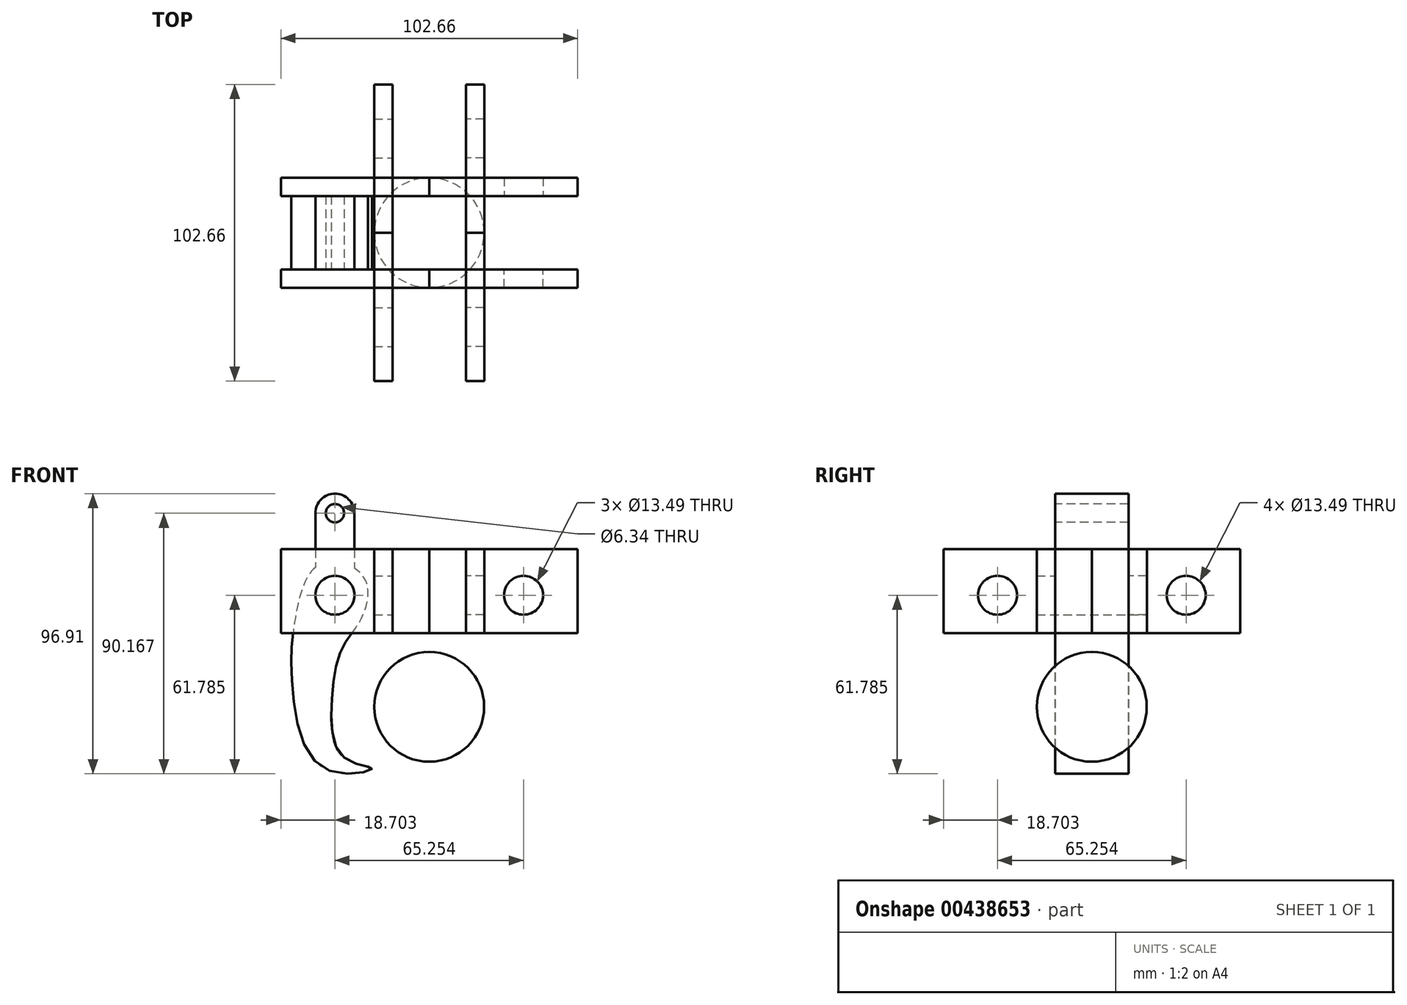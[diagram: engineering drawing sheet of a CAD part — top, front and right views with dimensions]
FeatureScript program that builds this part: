
annotation { "Feature Type Name" : "Feature", "Feature Type Description" : "" }
export const myFeature = defineFeature(function(context is Context, id is Id, definition is map)
    precondition{}
    {
        {
            var Q0;
            Q0=qCreatedBy(makeId("Front.planeOp"),FACE);
            var sketch = newSketch(context, id + "F0", { "sketchPlane" : qUnion([Q0])});
            skCircle(sketch, "E0", {"center": v(0, 0) * mm, "radius": 19 * mm});
            skFitSpline(sketch, "E1", {"points": [v(-14.63, -20) * mm, v(-23.81, -17.55) * mm, v(-30.46, 0) * mm, v(-28.59, 20.45) * mm, v(-23.1, 30.72) * mm, v(-23.1, 45.51) * mm, v(-38.56, 48.92) * mm, v(-45.55, 30.12) * mm, v(-45.15, 10.11) * mm, v(-30.93, -21.5) * mm, v(-14.63, -20) * mm]});
            skCircle(sketch, "E2", {"center": v(-32.63, 38.62) * mm, "radius": 6.75 * mm});
            skSolve(sketch);
        }
        {
            var Q0;
            Q0=makeQuery(id+"F0.imprint","IMPRINT",FACE,{"disambiguationData":[TD([[makeQuery(id+"F0.imprint","IMPRINT",EDGE,{"derivedFrom":sQuery(id+"F0.wireOp",EDGE,"E1")}),1.0]])]});
            extrude(context, id + "F1", {"entities" : qUnion([Q0]), "depth" : 12.7 * mm});
        }
        {
            var Q0;
            Q0=makeQuery(id+"F1.opExtrude","CAP_FACE",FACE,{"disambiguationData":[OSD([sQuery(id+"F0.wireOp",EDGE,"E1"),sQuery(id+"F0.wireOp",EDGE,"E2")])],"isStart":false});
            var sketch = newSketch(context, id + "F2", { "sketchPlane" : qUnion([Q0])});
            skLineSegment(sketch, "E3.bottom", {"start": v(0, 54.58) * mm, "end": v(-51.33, 54.58) * mm});
            skLineSegment(sketch, "E3.top", {"start": v(0, 25.55) * mm, "end": v(-51.33, 25.55) * mm});
            skLineSegment(sketch, "E3.left", {"start": v(0, 54.58) * mm, "end": v(0, 25.55) * mm});
            skLineSegment(sketch, "E3.right", {"start": v(-51.33, 54.58) * mm, "end": v(-51.33, 25.55) * mm});
            skSolve(sketch);
        }
        {
            var Q0;
            Q0=makeQuery(id+"F2.imprint","IMPRINT",FACE,{"disambiguationData":[TD([[makeQuery(id+"F2.imprint","IMPRINT",EDGE,{"derivedFrom":sQuery(id+"F2.wireOp",EDGE,"E3.bottom")}),1.0]])]});
            var Q1;
            Q1=makeQuery(id+"F2.imprint","IMPRINT",FACE,{"disambiguationData":[TD([[makeQuery(id+"F2.imprint","IMPRINT",EDGE,{"derivedFrom":makeQuery(id+"F1.opExtrude","CAP_EDGE",EDGE,{"disambiguationData":[OSD([sQuery(id+"F0.wireOp",EDGE,"E2")])],"isStart":false})}),-1.0]])]});
            extrude(context, id + "F3", {"entities" : qUnion([Q0, Q1]), "depth" : 6.35 * mm});
        }
        {
            var Q0;
            Q0=makeQuery(id+"F1.opExtrude","SWEPT_BODY",BODY,{"disambiguationData":[OSD([sQuery(id+"F0.wireOp",EDGE,"E1"),sQuery(id+"F0.wireOp",EDGE,"E2")])]});
            var Q1;
            Q1=makeQuery(id+"F3.opExtrude","SWEPT_BODY",BODY,{"disambiguationData":[OSD([sQuery(id+"F0.wireOp",EDGE,"E2"),sQuery(id+"F2.wireOp",EDGE,"E3.bottom"),sQuery(id+"F2.wireOp",EDGE,"E3.top"),sQuery(id+"F2.wireOp",EDGE,"E3.left"),sQuery(id+"F2.wireOp",EDGE,"E3.right")])]});
            var Q2;
            Q2=qCreatedBy(makeId("Front.planeOp"),FACE);
            mirror(context, id + "F4", {"entities" : qUnion([Q0, Q1]), "mirrorPlane" : qUnion([Q2])});
        }
        {
            var Q0;
            Q0=makeQuery(id+"F3.opExtrude","SWEPT_BODY",BODY,{"disambiguationData":[OSD([sQuery(id+"F0.wireOp",EDGE,"E2"),sQuery(id+"F2.wireOp",EDGE,"E3.bottom"),sQuery(id+"F2.wireOp",EDGE,"E3.top"),sQuery(id+"F2.wireOp",EDGE,"E3.left"),sQuery(id+"F2.wireOp",EDGE,"E3.right")])]});
            var Q1;
            Q1=makeQuery(id+"F4.opPattern","COPY",BODY,{"derivedFrom":makeQuery(id+"F3.opExtrude","SWEPT_BODY",BODY,{"disambiguationData":[OSD([sQuery(id+"F0.wireOp",EDGE,"E2"),sQuery(id+"F2.wireOp",EDGE,"E3.bottom"),sQuery(id+"F2.wireOp",EDGE,"E3.top"),sQuery(id+"F2.wireOp",EDGE,"E3.left"),sQuery(id+"F2.wireOp",EDGE,"E3.right")])]}),"instanceName":"1"});
            var Q2;
            Q2=qCreatedBy(makeId("Right.planeOp"),FACE);
            mirror(context, id + "F5", {"entities" : qUnion([Q0, Q1]), "mirrorPlane" : qUnion([Q2])});
        }
        {
            var Q0;
            Q0=qCreatedBy(makeId("Front.planeOp"),FACE);
            var sketch = newSketch(context, id + "F6", { "sketchPlane" : qUnion([Q0])});
            skLineSegment(sketch, "E4", {"start": v(0, 0) * mm, "end": v(0, 97.35) * mm, "construction": true});
            skSolve(sketch);
        }
        {
            var Q0;
            Q0=makeQuery(id+"F3.opExtrude","SWEPT_BODY",BODY,{"disambiguationData":[OSD([sQuery(id+"F0.wireOp",EDGE,"E2"),sQuery(id+"F2.wireOp",EDGE,"E3.bottom"),sQuery(id+"F2.wireOp",EDGE,"E3.top"),sQuery(id+"F2.wireOp",EDGE,"E3.left"),sQuery(id+"F2.wireOp",EDGE,"E3.right")])]});
            var Q1;
            Q1=makeQuery(id+"F4.opPattern","COPY",BODY,{"derivedFrom":makeQuery(id+"F3.opExtrude","SWEPT_BODY",BODY,{"disambiguationData":[OSD([sQuery(id+"F0.wireOp",EDGE,"E2"),sQuery(id+"F2.wireOp",EDGE,"E3.bottom"),sQuery(id+"F2.wireOp",EDGE,"E3.top"),sQuery(id+"F2.wireOp",EDGE,"E3.left"),sQuery(id+"F2.wireOp",EDGE,"E3.right")])]}),"instanceName":"1"});
            var Q2;
            Q2=sQuery(id+"F6.wireOp",EDGE,"E4");
            circularPattern(context, id + "F7", {"entities" : qUnion([Q0, Q1]), "axis" : qUnion([Q2]), "angle" : 360 * degree, "instanceCount" : 4, "equalSpace" : true});
        }
        {
            var Q0;
            Q0=qCreatedBy(makeId("Front.planeOp"),FACE);
            var sketch = newSketch(context, id + "F8", { "sketchPlane" : qUnion([Q0])});
            skCircle(sketch, "E5", {"center": v(0, 0) * mm, "radius": 19 * mm});
            skLineSegment(sketch, "E6", {"start": v(0, 19) * mm, "end": v(0, -19) * mm});
            skSolve(sketch);
        }
        {
            var Q0;
            {var subQ0=sQuery(id+"F8.wireOp",EDGE,"E6");Q0=makeQuery(id+"F8.imprint","IMPRINT",FACE,{"disambiguationData":[TD([[makeQuery(id+"F8.imprint","IMPRINT",EDGE,{"derivedFrom":subQ0}),1.0]])]});}
            var Q1;
            Q1=sQuery(id+"F8.wireOp",EDGE,"E6");
            revolve(context, id + "F9", {"entities" : qUnion([Q0]), "axis" : qUnion([Q1]), "revolveType" : RevolveType.FULL});
        }
        {
            var Q0;
            Q0=makeQuery(id+"F4.opPattern","COPY",BODY,{"derivedFrom":makeQuery(id+"F1.opExtrude","SWEPT_BODY",BODY,{"disambiguationData":[OSD([sQuery(id+"F0.wireOp",EDGE,"E1"),sQuery(id+"F0.wireOp",EDGE,"E2")])]}),"instanceName":"1"});
            var Q1;
            Q1=makeQuery(id+"F1.opExtrude","SWEPT_BODY",BODY,{"disambiguationData":[OSD([sQuery(id+"F0.wireOp",EDGE,"E1"),sQuery(id+"F0.wireOp",EDGE,"E2")])]});
            booleanBodies(context, id + "F10", {"operationType" : BooleanOperationType.UNION, "tools" : qUnion([Q0, Q1])});
        }
        {
            var Q0;
            Q0=makeQuery(id+"F7.opPattern","COPY",BODY,{"derivedFrom":makeQuery(id+"F3.opExtrude","SWEPT_BODY",BODY,{"disambiguationData":[OSD([sQuery(id+"F0.wireOp",EDGE,"E2"),sQuery(id+"F2.wireOp",EDGE,"E3.bottom"),sQuery(id+"F2.wireOp",EDGE,"E3.top"),sQuery(id+"F2.wireOp",EDGE,"E3.left"),sQuery(id+"F2.wireOp",EDGE,"E3.right")])]}),"instanceName":"2"});
            deleteBodies(context, id + "F11", {"entities" : qUnion([Q0])});
        }
        {
            var Q0;
            Q0=makeQuery(id+"F7.opPattern","COPY",BODY,{"derivedFrom":makeQuery(id+"F4.opPattern","COPY",BODY,{"derivedFrom":makeQuery(id+"F3.opExtrude","SWEPT_BODY",BODY,{"disambiguationData":[OSD([sQuery(id+"F0.wireOp",EDGE,"E2"),sQuery(id+"F2.wireOp",EDGE,"E3.bottom"),sQuery(id+"F2.wireOp",EDGE,"E3.top"),sQuery(id+"F2.wireOp",EDGE,"E3.left"),sQuery(id+"F2.wireOp",EDGE,"E3.right")])]}),"instanceName":"1"}),"instanceName":"2"});
            deleteBodies(context, id + "F12", {"entities" : qUnion([Q0])});
        }
        {
            var Q0;
            Q0=makeQuery(id+"F4.opPattern","COPY",BODY,{"derivedFrom":makeQuery(id+"F1.opExtrude","SWEPT_BODY",BODY,{"disambiguationData":[OSD([sQuery(id+"F0.wireOp",EDGE,"E1"),sQuery(id+"F0.wireOp",EDGE,"E2")])]}),"instanceName":"1"});
            var Q1;
            Q1=makeQuery(id+"F1.opExtrude","CAP_EDGE",EDGE,{"disambiguationData":[OSD([sQuery(id+"F0.wireOp",EDGE,"E2")])],"isStart":false});
            transform(context, id + "F13", {"entities" : qUnion([Q0]), "transformType" : TransformType.ROTATION, "transformAxis" : qUnion([Q1]), "angle" : 5 * degree, "oppositeDirection" : true, "makeCopy" : false});
        }
        {
            var Q0;
            Q0=makeQuery(id+"F1.opExtrude","CAP_FACE",FACE,{"disambiguationData":[OSD([sQuery(id+"F0.wireOp",EDGE,"E1"),sQuery(id+"F0.wireOp",EDGE,"E2")])],"isStart":false});
            var sketch = newSketch(context, id + "F14", { "sketchPlane" : qUnion([Q0])});
            skCircle(sketch, "E7", {"center": v(-32.63, 67) * mm, "radius": 6.75 * mm});
            skLineSegment(sketch, "E8", {"start": v(-32.63, 67) * mm, "end": v(-32.63, 38.62) * mm, "construction": true});
            skLineSegment(sketch, "E9", {"start": v(-39.37, 67) * mm, "end": v(-39.37, 38.62) * mm});
            skLineSegment(sketch, "E10", {"start": v(-25.88, 67) * mm, "end": v(-25.88, 38.62) * mm});
            skCircle(sketch, "E11", {"center": v(-32.63, 67) * mm, "radius": 3.17 * mm});
            skSolve(sketch);
        }
        {
            var Q0;
            {var subQ0=sQuery(id+"F14.wireOp",EDGE,"E9");var subQ1=sQuery(id+"F14.wireOp",EDGE,"E7");var subQ2=makeQuery(id+"F14.imprint","INTERSECT",VERTEX,{"derivedFrom":[subQ1,subQ0]});Q0=makeQuery(id+"F14.imprint","IMPRINT",FACE,{"disambiguationData":[TD([[makeQuery(id+"F14.imprint","IMPRINT",EDGE,{"disambiguationData":[TD([[subQ2,-1.0]])],"derivedFrom":subQ1}),-1.0]])]});}
            var Q1;
            {var subQ0=sQuery(id+"F14.wireOp",EDGE,"E7");var subQ1=makeQuery(id+"F14.imprint","INTERSECT",VERTEX,{"derivedFrom":[subQ0,sQuery(id+"F14.wireOp",EDGE,"E9")]});Q1=makeQuery(id+"F14.imprint","IMPRINT",FACE,{"disambiguationData":[TD([[makeQuery(id+"F14.imprint","IMPRINT",EDGE,{"disambiguationData":[TD([[subQ1,1.0]])],"derivedFrom":subQ0}),1.0]])]});}
            extrude(context, id + "F15", {"entities" : qUnion([Q0, Q1]), "operationType" : NewBodyOperationType.ADD, "oppositeDirection" : true, "depth" : 25.4 * mm});
        }
    });
